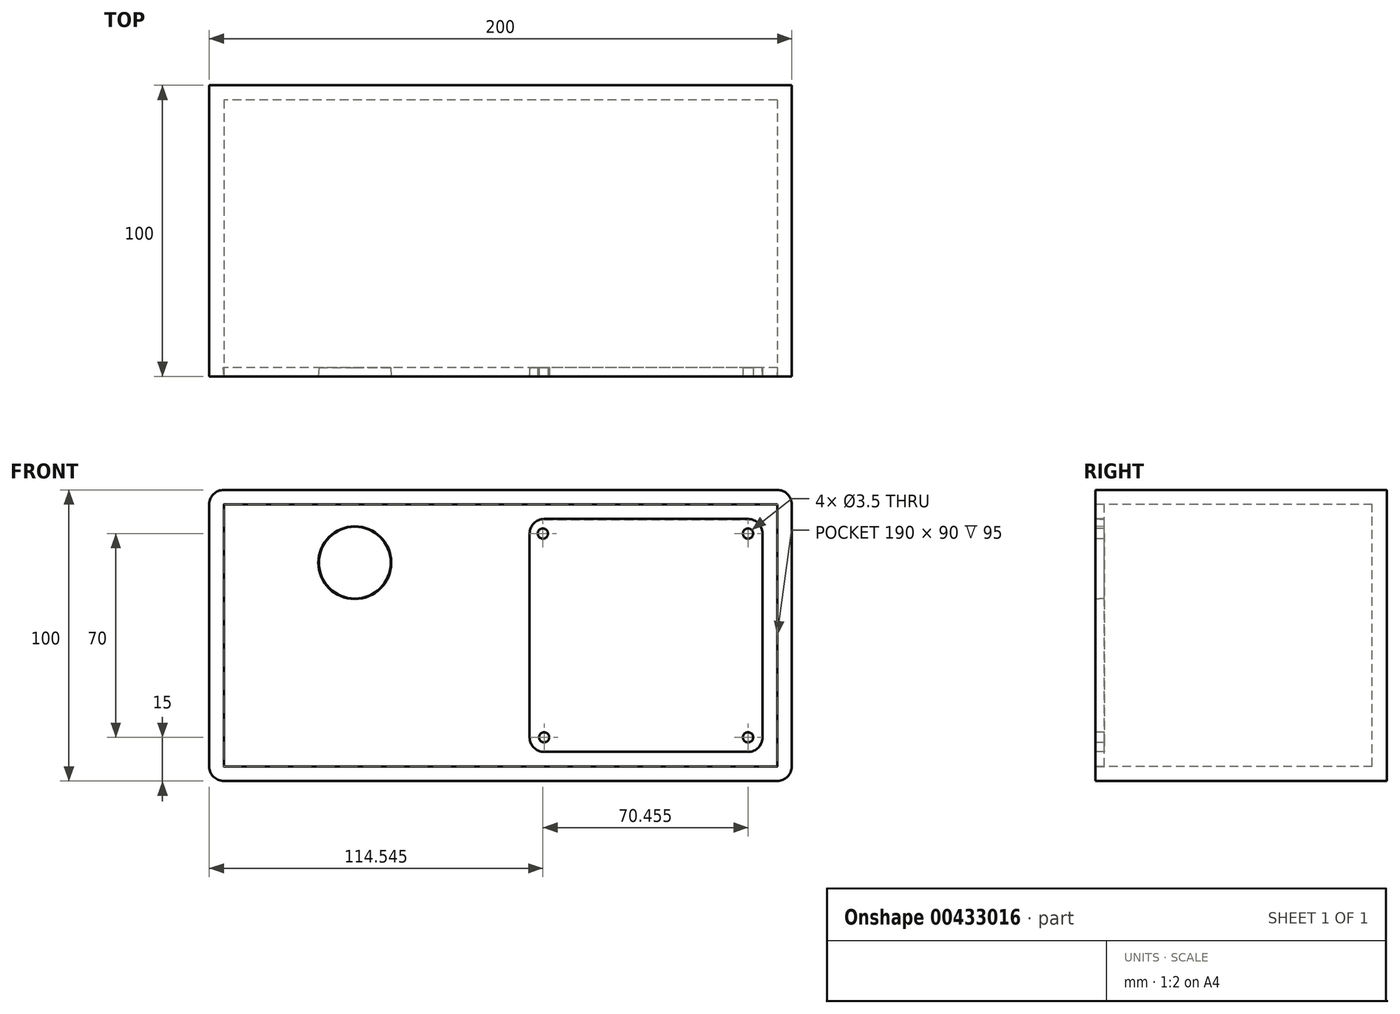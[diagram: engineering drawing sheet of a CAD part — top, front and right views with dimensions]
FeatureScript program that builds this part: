
annotation { "Feature Type Name" : "Feature", "Feature Type Description" : "" }
export const myFeature = defineFeature(function(context is Context, id is Id, definition is map)
    precondition{}
    {
        {
            var Q0;
            Q0=qCreatedBy(makeId("Front.planeOp"),FACE);
            var sketch = newSketch(context, id + "F0", { "sketchPlane" : qUnion([Q0])});
            skLineSegment(sketch, "E0.bottom", {"start": v(100, -75) * mm, "end": v(-100, -75) * mm});
            skLineSegment(sketch, "E0.top", {"start": v(100, 25) * mm, "end": v(-100, 25) * mm});
            skLineSegment(sketch, "E0.left", {"start": v(100, -75) * mm, "end": v(100, 25) * mm});
            skLineSegment(sketch, "E0.right", {"start": v(-100, -75) * mm, "end": v(-100, 25) * mm});
            skPoint(sketch, "E0.middle", {"position": v(0, 0) * mm});
            skSolve(sketch);
        }
        {
            var Q0;
            Q0=makeQuery(id+"F0.imprint","IMPRINT",FACE,{"disambiguationData":[TD([[makeQuery(id+"F0.imprint","IMPRINT",EDGE,{"derivedFrom":sQuery(id+"F0.wireOp",EDGE,"E0.bottom")}),-1.0]])]});
            extrude(context, id + "F1", {"entities" : qUnion([Q0]), "depth" : 100 * mm, "offsetDistance" : 25 * mm});
        }
        {
            var Q0;
            Q0=makeQuery(id+"F1.opExtrude","SWEPT_EDGE",EDGE,{"disambiguationData":[OSD([sQuery(id+"F0.wireOp",EDGE,"E0.top"),sQuery(id+"F0.wireOp",EDGE,"E0.left")])]});
            var Q1;
            Q1=makeQuery(id+"F1.opExtrude","SWEPT_EDGE",EDGE,{"disambiguationData":[OSD([sQuery(id+"F0.wireOp",EDGE,"E0.bottom"),sQuery(id+"F0.wireOp",EDGE,"E0.left")])]});
            var Q2;
            Q2=makeQuery(id+"F1.opExtrude","SWEPT_EDGE",EDGE,{"disambiguationData":[OSD([sQuery(id+"F0.wireOp",EDGE,"E0.bottom"),sQuery(id+"F0.wireOp",EDGE,"E0.right")])]});
            var Q3;
            Q3=makeQuery(id+"F1.opExtrude","SWEPT_EDGE",EDGE,{"disambiguationData":[OSD([sQuery(id+"F0.wireOp",EDGE,"E0.top"),sQuery(id+"F0.wireOp",EDGE,"E0.right")])]});
            fillet(context, id + "F2", {"entities" : qUnion([Q0, Q1, Q2, Q3]), "radius" : 5 * mm, "tangentPropagation" : true, "allowEdgeOverflow" : false});
        }
        {
            var Q0;
            Q0=makeQuery(id+"F1.opExtrude","CAP_FACE",FACE,{"disambiguationData":[OSD([sQuery(id+"F0.wireOp",EDGE,"E0.bottom"),sQuery(id+"F0.wireOp",EDGE,"E0.top"),sQuery(id+"F0.wireOp",EDGE,"E0.left"),sQuery(id+"F0.wireOp",EDGE,"E0.right")])],"isStart":false});
            shell(context, id + "F3", {"entities" : qUnion([Q0]), "thickness" : 5 * mm});
        }
        {
            var Q0;
            Q0=makeQuery(id+"F1.opExtrude","CAP_FACE",FACE,{"disambiguationData":[OSD([sQuery(id+"F0.wireOp",EDGE,"E0.bottom"),sQuery(id+"F0.wireOp",EDGE,"E0.top"),sQuery(id+"F0.wireOp",EDGE,"E0.left"),sQuery(id+"F0.wireOp",EDGE,"E0.right")])],"isStart":false});
            var sketch = newSketch(context, id + "F4", { "sketchPlane" : qUnion([Q0])});
            skLineSegment(sketch, "E1.bottom", {"start": v(-95, 20) * mm, "end": v(95, 20) * mm});
            skLineSegment(sketch, "E1.top", {"start": v(-95, -70) * mm, "end": v(95, -70) * mm});
            skLineSegment(sketch, "E1.left", {"start": v(-95, 20) * mm, "end": v(-95, -70) * mm});
            skLineSegment(sketch, "E1.right", {"start": v(95, 20) * mm, "end": v(95, -70) * mm});
            skPoint(sketch, "E2", {"position": v(50, -25) * mm});
            skLineSegment(sketch, "E3.bottom", {"start": v(85, -65) * mm, "end": v(15, -65) * mm});
            skLineSegment(sketch, "E3.top", {"start": v(85, 15) * mm, "end": v(15, 15) * mm});
            skLineSegment(sketch, "E3.left", {"start": v(90, -60) * mm, "end": v(90, 10) * mm});
            skLineSegment(sketch, "E3.right", {"start": v(10, -60) * mm, "end": v(10, 10) * mm});
            skPoint(sketch, "E4.visualSharp", {"position": v(10, 15) * mm});
            skArc(sketch, "E4.filletArc", {"start": v(15, 15) * mm, "mid": v(11.46, 13.54) * mm, "end": v(10, 10) * mm});
            skPoint(sketch, "E5.visualSharp", {"position": v(90, 15) * mm});
            skArc(sketch, "E5.filletArc", {"start": v(90, 10) * mm, "mid": v(88.54, 13.54) * mm, "end": v(85, 15) * mm});
            skPoint(sketch, "E6.visualSharp", {"position": v(90, -65) * mm});
            skArc(sketch, "E6.filletArc", {"start": v(85, -65) * mm, "mid": v(88.54, -63.54) * mm, "end": v(90, -60) * mm});
            skPoint(sketch, "E7.visualSharp", {"position": v(10, -65) * mm});
            skArc(sketch, "E7.filletArc", {"start": v(10, -60) * mm, "mid": v(11.46, -63.54) * mm, "end": v(15, -65) * mm});
            skCircle(sketch, "E8", {"center": v(14.55, 10) * mm, "radius": 1.75 * mm});
            skCircle(sketch, "E9", {"center": v(85, 10) * mm, "radius": 1.75 * mm});
            skCircle(sketch, "E10", {"center": v(15, -60) * mm, "radius": 1.75 * mm});
            skCircle(sketch, "E11", {"center": v(85, -60) * mm, "radius": 1.75 * mm});
            skPoint(sketch, "E12.MirrorP", {"position": v(-50, 0) * mm});
            skCircle(sketch, "E13", {"center": v(-50, 0) * mm, "radius": 12.5 * mm});
            skSolve(sketch);
        }
        {
            var Q0;
            Q0=makeQuery(id+"F4.imprint","IMPRINT",FACE,{"disambiguationData":[TD([[makeQuery(id+"F4.imprint","IMPRINT",EDGE,{"derivedFrom":sQuery(id+"F4.wireOp",EDGE,"E1.bottom")}),1.0]])]});
            extrude(context, id + "F5", {"entities" : qUnion([Q0]), "oppositeDirection" : true, "depth" : 3 * mm, "offsetDistance" : 25 * mm, "hasDraft" : true, "draftAngle" : 3 * degree});
        }
        {
            var Q0;
            Q0=makeQuery(id+"F4.imprint","IMPRINT",FACE,{"disambiguationData":[TD([[makeQuery(id+"F4.imprint","IMPRINT",EDGE,{"derivedFrom":sQuery(id+"F4.wireOp",EDGE,"E3.bottom")}),-1.0]])]});
            extrude(context, id + "F6", {"entities" : qUnion([Q0]), "oppositeDirection" : true, "depth" : 3 * mm, "offsetDistance" : 25 * mm});
        }
    });
